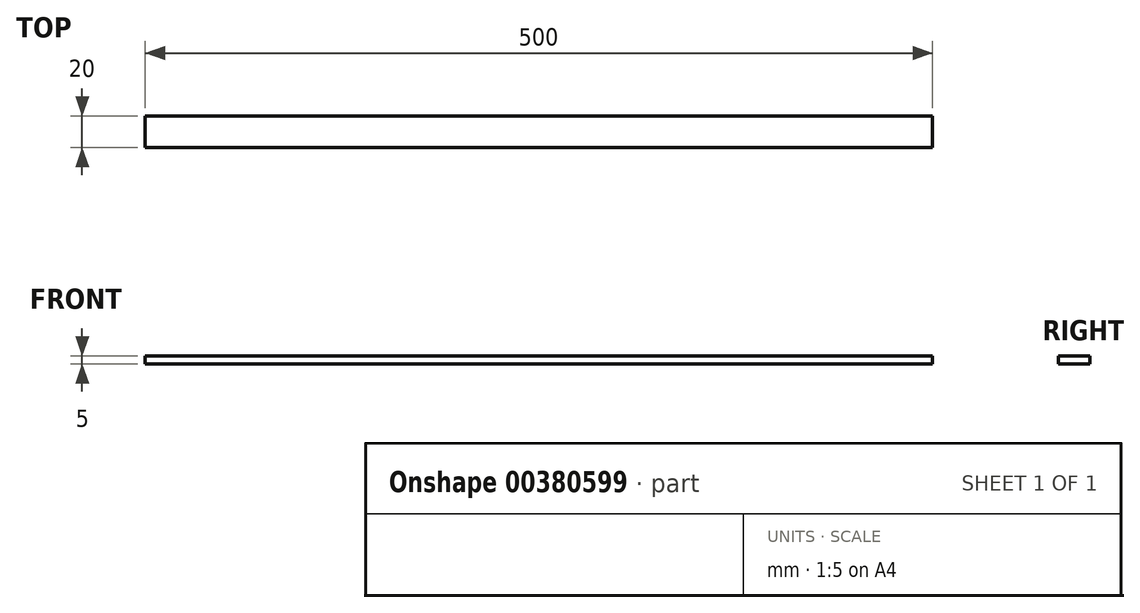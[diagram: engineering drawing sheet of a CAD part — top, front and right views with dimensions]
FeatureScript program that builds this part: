
annotation { "Feature Type Name" : "Feature", "Feature Type Description" : "" }
export const myFeature = defineFeature(function(context is Context, id is Id, definition is map)
    precondition{}
    {
        {
            var Q0;
            Q0=qCreatedBy(makeId("Top.planeOp"),FACE);
            var sketch = newSketch(context, id + "F0", { "sketchPlane" : qUnion([Q0])});
            skLineSegment(sketch, "E0.bottom", {"start": v(250, 10) * mm, "end": v(-250, 10) * mm});
            skLineSegment(sketch, "E0.top", {"start": v(250, -10) * mm, "end": v(-250, -10) * mm});
            skLineSegment(sketch, "E0.left", {"start": v(250, 10) * mm, "end": v(250, -10) * mm});
            skLineSegment(sketch, "E0.right", {"start": v(-250, 10) * mm, "end": v(-250, -10) * mm});
            skPoint(sketch, "E0.middle", {"position": v(0, 0) * mm});
            skSolve(sketch);
        }
        {
            var Q0;
            Q0 = qSketchRegion(id + "F0", true);
            extrude(context, id + "F1", {"entities" : qUnion([Q0]), "depth" : 5 * mm});
        }
    });
